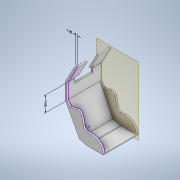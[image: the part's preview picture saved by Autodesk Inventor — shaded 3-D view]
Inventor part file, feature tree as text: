
AUTODESK INVENTOR PART (.ipt)
format: ipt  version: 2021 (Build 250183000, 183)  size: 202,240 bytes
history: native  units: in
note: dims shown in document units (in); Inventor stores cm internally (conversion verified against a paired STEP export)
features: sketch x6, extrude x4, other x3, plane x1
ambient origin geometry x8: Origin, YZ Plane, XZ Plane, XY Plane, X Axis, Y Axis, Z Axis, Center Point
bodies: Solid1 (feature_tree)
feature tree (14):
  other  "Annotations"
  sketch  "Sketch1"  dims[d63=0.5in d64=0.5in]
  extrude  "Extrusion1"  Depth=0.5in
  extrude  "Extrusion2"  Depth=0.5in
  plane  "Work Plane3"
  sketch  "Sketch5"  dims[d68=0.5in d69=18.5in d70=0.0in]
  sketch  "Sketch6"  dims[d71=1.0in d72=0.0in d73=-18.5in]
  extrude  "Extrusion3"  Depth=18.5in TaperAngle=0.0deg
  extrude  "Extrusion4"  [1 undecoded]
  sketch  "Sketch4"  dims[d65=0.5in d66=0.5in]
  sketch  "Sketch7"  dims[d74=1.0in d75=0.0in]
  sketch  "Sketch8"  dims[d77=9.0in d78=23.5in d80=5.25in d81=5.25in d82=20.0in d83=10.5in d84=1.0in d85=1.875in d86=1.875in d87=36.0in d88=0.0in d57=1.0004in d76=9.0in d24=0.5in d25=0.0344in d26=0.5in d27=0.0344in]
  other  "Linear Dimension 1"
  other  "Linear Dimension 2"
note: 1 required parameter value undecoded (feature->parameter linkage not recoverable at this tier; creation-order binding heuristic only, values carry confidence <= 0.55)
